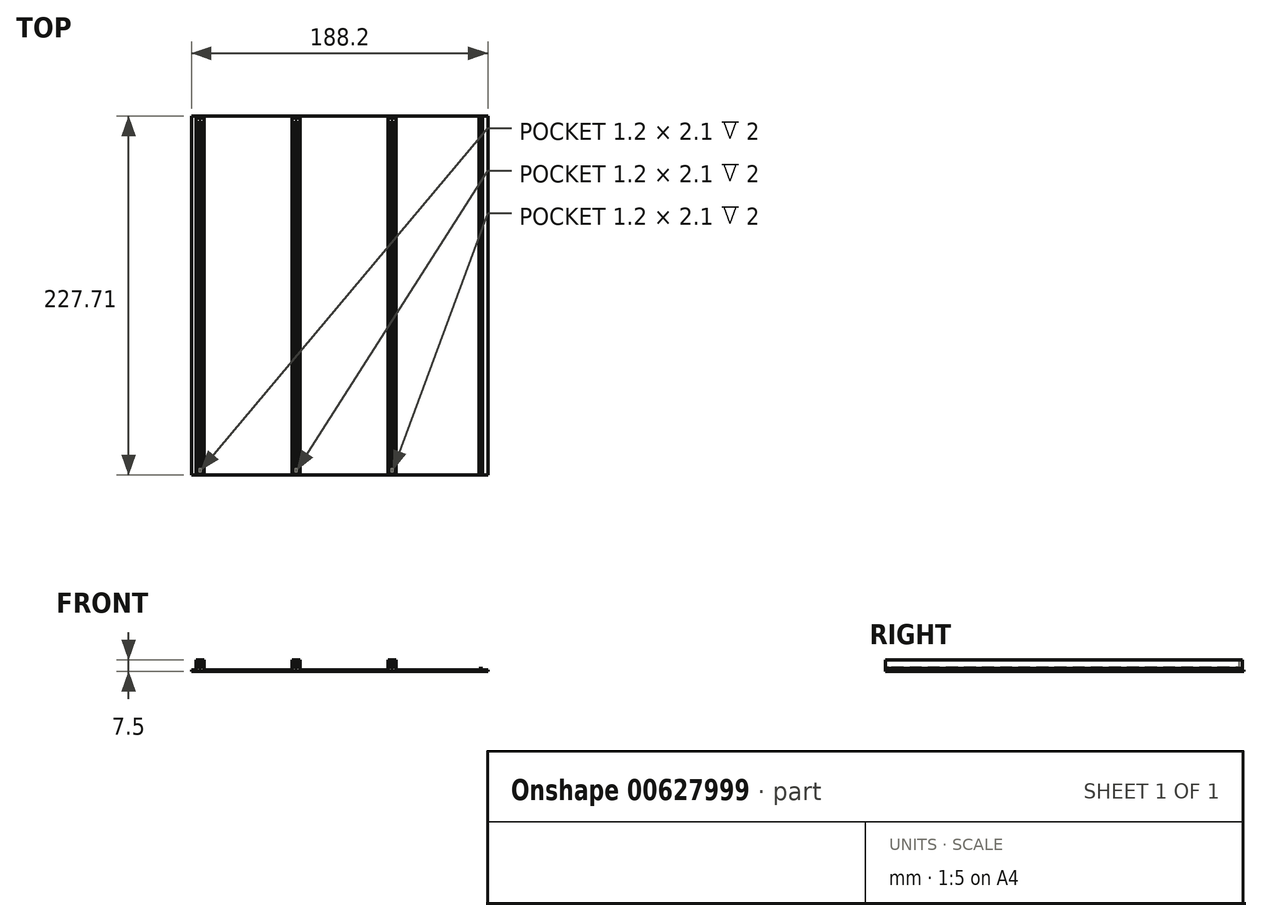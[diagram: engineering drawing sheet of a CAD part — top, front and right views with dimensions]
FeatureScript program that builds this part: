
annotation { "Feature Type Name" : "Feature", "Feature Type Description" : "" }
export const myFeature = defineFeature(function(context is Context, id is Id, definition is map)
    precondition{}
    {
        {
            var Q0;
            Q0=qCreatedBy(makeId("Top.planeOp"),FACE);
            var sketch = newSketch(context, id + "F0", { "sketchPlane" : qUnion([Q0])});
            skLineSegment(sketch, "E0.bottom", {"start": v(0, 0) * mm, "end": v(5.2, 0) * mm});
            skLineSegment(sketch, "E0.top", {"start": v(0, 226.71) * mm, "end": v(5.2, 226.71) * mm});
            skLineSegment(sketch, "E0.left", {"start": v(0, 0) * mm, "end": v(0, 226.71) * mm});
            skLineSegment(sketch, "E0.right", {"start": v(5.2, 0) * mm, "end": v(5.2, 226.71) * mm});
            skLineSegment(sketch, "E1.1.0.0", {"start": v(66.2, 0) * mm, "end": v(66.2, 226.71) * mm});
            skLineSegment(sketch, "E1.1.0.1", {"start": v(61, 0) * mm, "end": v(61, 226.71) * mm});
            skLineSegment(sketch, "E1.1.0.2", {"start": v(61, 226.71) * mm, "end": v(66.2, 226.71) * mm});
            skLineSegment(sketch, "E1.1.0.3", {"start": v(61, 0) * mm, "end": v(66.2, 0) * mm});
            skLineSegment(sketch, "E1.2.0.0", {"start": v(127.2, 0) * mm, "end": v(127.2, 226.71) * mm});
            skLineSegment(sketch, "E1.2.0.1", {"start": v(122, 0) * mm, "end": v(122, 226.71) * mm});
            skLineSegment(sketch, "E1.2.0.2", {"start": v(122, 226.71) * mm, "end": v(127.2, 226.71) * mm});
            skLineSegment(sketch, "E1.2.0.3", {"start": v(122, 0) * mm, "end": v(127.2, 0) * mm});
            skLineSegment(sketch, "E1.direction1", {"start": v(0, 0) * mm, "end": v(61, 0) * mm, "construction": true});
            skSolve(sketch);
        }
        {
            var Q0;
            Q0=makeQuery(id+"F0.imprint","IMPRINT",FACE,{"disambiguationData":[TD([[makeQuery(id+"F0.imprint","IMPRINT",EDGE,{"derivedFrom":sQuery(id+"F0.wireOp",EDGE,"E0.bottom")}),1.0]])]});
            var Q1;
            Q1=makeQuery(id+"F0.imprint","IMPRINT",FACE,{"disambiguationData":[TD([[makeQuery(id+"F0.imprint","IMPRINT",EDGE,{"derivedFrom":sQuery(id+"F0.wireOp",EDGE,"E1.1.0.0")}),1.0]])]});
            var Q2;
            Q2=makeQuery(id+"F0.imprint","IMPRINT",FACE,{"disambiguationData":[TD([[makeQuery(id+"F0.imprint","IMPRINT",EDGE,{"derivedFrom":sQuery(id+"F0.wireOp",EDGE,"E1.2.0.0")}),1.0]])]});
            extrude(context, id + "F1", {"entities" : qUnion([Q0, Q1, Q2]), "depth" : 2 * mm, "offsetDistance" : 25 * mm});
        }
        {
            var Q0;
            Q0=makeQuery(id+"F1.opExtrude","CAP_FACE",FACE,{"disambiguationData":[OSD([sQuery(id+"F0.wireOp",EDGE,"E0.bottom"),sQuery(id+"F0.wireOp",EDGE,"E0.top"),sQuery(id+"F0.wireOp",EDGE,"E0.left"),sQuery(id+"F0.wireOp",EDGE,"E0.right")])],"isStart":false});
            var sketch = newSketch(context, id + "F2", { "sketchPlane" : qUnion([Q0])});
            skLineSegment(sketch, "E2.bottom", {"start": v(0, 0) * mm, "end": v(2, 0) * mm});
            skLineSegment(sketch, "E2.top", {"start": v(0, 226.71) * mm, "end": v(5.2, 226.71) * mm});
            skLineSegment(sketch, "E2.left", {"start": v(0, 0) * mm, "end": v(0, 226.71) * mm});
            skLineSegment(sketch, "E2.right", {"start": v(5.2, 0) * mm, "end": v(5.2, 226.71) * mm});
            skLineSegment(sketch, "E3.top", {"start": v(2, 224.71) * mm, "end": v(3.2, 224.71) * mm});
            skLineSegment(sketch, "E3.left", {"start": v(2, 0) * mm, "end": v(2, 224.71) * mm});
            skLineSegment(sketch, "E3.right", {"start": v(3.2, 0) * mm, "end": v(3.2, 224.71) * mm});
            skLineSegment(sketch, "E4.trimOffspring", {"start": v(3.2, 0) * mm, "end": v(5.2, 0) * mm});
            skLineSegment(sketch, "E5.1.0.0", {"start": v(61, 0) * mm, "end": v(61, 226.71) * mm});
            skLineSegment(sketch, "E5.1.0.1", {"start": v(66.2, 0) * mm, "end": v(66.2, 226.71) * mm});
            skLineSegment(sketch, "E5.1.0.2", {"start": v(63, 0) * mm, "end": v(63, 224.71) * mm});
            skLineSegment(sketch, "E5.1.0.3", {"start": v(64.2, 0) * mm, "end": v(64.2, 224.71) * mm});
            skLineSegment(sketch, "E5.1.0.4", {"start": v(64.2, 0) * mm, "end": v(66.2, 0) * mm});
            skLineSegment(sketch, "E5.1.0.5", {"start": v(61, 226.71) * mm, "end": v(66.2, 226.71) * mm});
            skLineSegment(sketch, "E5.1.0.6", {"start": v(61, 0) * mm, "end": v(63, 0) * mm});
            skLineSegment(sketch, "E5.1.0.7", {"start": v(63, 224.71) * mm, "end": v(64.2, 224.71) * mm});
            skLineSegment(sketch, "E5.2.0.0", {"start": v(122, 0) * mm, "end": v(122, 226.71) * mm});
            skLineSegment(sketch, "E5.2.0.1", {"start": v(127.2, 0) * mm, "end": v(127.2, 226.71) * mm});
            skLineSegment(sketch, "E5.2.0.2", {"start": v(124, 0) * mm, "end": v(124, 224.71) * mm});
            skLineSegment(sketch, "E5.2.0.3", {"start": v(125.2, 0) * mm, "end": v(125.2, 224.71) * mm});
            skLineSegment(sketch, "E5.2.0.4", {"start": v(125.2, 0) * mm, "end": v(127.2, 0) * mm});
            skLineSegment(sketch, "E5.2.0.5", {"start": v(122, 226.71) * mm, "end": v(127.2, 226.71) * mm});
            skLineSegment(sketch, "E5.2.0.6", {"start": v(122, 0) * mm, "end": v(124, 0) * mm});
            skLineSegment(sketch, "E5.2.0.7", {"start": v(124, 224.71) * mm, "end": v(125.2, 224.71) * mm});
            skLineSegment(sketch, "E5.direction1", {"start": v(0, 0) * mm, "end": v(61, 0) * mm, "construction": true});
            skSolve(sketch);
        }
        {
            var Q0;
            Q0=makeQuery(id+"F2.imprint","IMPRINT",FACE,{"disambiguationData":[TD([[makeQuery(id+"F2.imprint","IMPRINT",EDGE,{"derivedFrom":sQuery(id+"F2.wireOp",EDGE,"E2.bottom")}),1.0]])]});
            var Q1;
            Q1=makeQuery(id+"F2.imprint","IMPRINT",FACE,{"disambiguationData":[TD([[makeQuery(id+"F2.imprint","IMPRINT",EDGE,{"derivedFrom":sQuery(id+"F2.wireOp",EDGE,"E5.1.0.0")}),-1.0]])]});
            var Q2;
            Q2=makeQuery(id+"F2.imprint","IMPRINT",FACE,{"disambiguationData":[TD([[makeQuery(id+"F2.imprint","IMPRINT",EDGE,{"derivedFrom":sQuery(id+"F2.wireOp",EDGE,"E5.2.0.0")}),-1.0]])]});
            extrude(context, id + "F3", {"entities" : qUnion([Q0, Q1, Q2]), "operationType" : NewBodyOperationType.ADD, "depth" : 4.5 * mm, "offsetDistance" : 25 * mm});
        }
        {
            var Q0;
            Q0=makeQuery(id+"F1.opExtrude","CAP_FACE",FACE,{"disambiguationData":[OSD([sQuery(id+"F0.wireOp",EDGE,"E0.bottom"),sQuery(id+"F0.wireOp",EDGE,"E0.top"),sQuery(id+"F0.wireOp",EDGE,"E0.left"),sQuery(id+"F0.wireOp",EDGE,"E0.right")])],"isStart":false});
            var sketch = newSketch(context, id + "F4", { "sketchPlane" : qUnion([Q0])});
            skLineSegment(sketch, "E6.bottom", {"start": v(2, 1.9) * mm, "end": v(3.2, 1.9) * mm});
            skLineSegment(sketch, "E6.top", {"start": v(2, 4) * mm, "end": v(3.2, 4) * mm});
            skLineSegment(sketch, "E6.left", {"start": v(2, 1.9) * mm, "end": v(2, 4) * mm});
            skLineSegment(sketch, "E6.right", {"start": v(3.2, 1.9) * mm, "end": v(3.2, 4) * mm});
            skLineSegment(sketch, "E7.1.0.0", {"start": v(63, 1.9) * mm, "end": v(64.2, 1.9) * mm});
            skLineSegment(sketch, "E7.1.0.1", {"start": v(63, 1.9) * mm, "end": v(63, 4) * mm});
            skLineSegment(sketch, "E7.1.0.2", {"start": v(63, 4) * mm, "end": v(64.2, 4) * mm});
            skLineSegment(sketch, "E7.1.0.3", {"start": v(64.2, 1.9) * mm, "end": v(64.2, 4) * mm});
            skLineSegment(sketch, "E7.2.0.0", {"start": v(124, 1.9) * mm, "end": v(125.2, 1.9) * mm});
            skLineSegment(sketch, "E7.2.0.1", {"start": v(124, 1.9) * mm, "end": v(124, 4) * mm});
            skLineSegment(sketch, "E7.2.0.2", {"start": v(124, 4) * mm, "end": v(125.2, 4) * mm});
            skLineSegment(sketch, "E7.2.0.3", {"start": v(125.2, 1.9) * mm, "end": v(125.2, 4) * mm});
            skLineSegment(sketch, "E7.direction1", {"start": v(2, 1.9) * mm, "end": v(63, 1.9) * mm, "construction": true});
            skSolve(sketch);
        }
        {
            var Q0;
            Q0=makeQuery(id+"F4.imprint","IMPRINT",FACE,{"disambiguationData":[TD([[makeQuery(id+"F4.imprint","IMPRINT",EDGE,{"derivedFrom":sQuery(id+"F4.wireOp",EDGE,"E6.bottom")}),1.0]])]});
            var Q1;
            Q1=makeQuery(id+"F4.imprint","IMPRINT",FACE,{"disambiguationData":[TD([[makeQuery(id+"F4.imprint","IMPRINT",EDGE,{"derivedFrom":sQuery(id+"F4.wireOp",EDGE,"E7.1.0.0")}),1.0]])]});
            var Q2;
            Q2=makeQuery(id+"F4.imprint","IMPRINT",FACE,{"disambiguationData":[TD([[makeQuery(id+"F4.imprint","IMPRINT",EDGE,{"derivedFrom":sQuery(id+"F4.wireOp",EDGE,"E7.2.0.0")}),1.0]])]});
            extrude(context, id + "F5", {"entities" : qUnion([Q0, Q1, Q2]), "operationType" : NewBodyOperationType.REMOVE, "oppositeDirection" : true, "depth" : 25 * mm, "offsetDistance" : 25 * mm});
        }
        {
            var Q0;
            Q0=qCreatedBy(makeId("Top.planeOp"),FACE);
            var sketch = newSketch(context, id + "F6", { "sketchPlane" : qUnion([Q0])});
            skLineSegment(sketch, "E8.bottom", {"start": v(0, 0) * mm, "end": v(185.5, 0) * mm});
            skLineSegment(sketch, "E8.top", {"start": v(0, 227.71) * mm, "end": v(185.5, 227.71) * mm});
            skLineSegment(sketch, "E8.left", {"start": v(0, 0) * mm, "end": v(0, 227.71) * mm});
            skLineSegment(sketch, "E8.right", {"start": v(185.5, 0) * mm, "end": v(185.5, 227.71) * mm});
            skLineSegment(sketch, "E9.bottom", {"start": v(0, 0) * mm, "end": v(-2.7, 0) * mm});
            skLineSegment(sketch, "E9.top", {"start": v(0, 227.71) * mm, "end": v(-2.7, 227.71) * mm});
            skLineSegment(sketch, "E9.right", {"start": v(-2.7, 0) * mm, "end": v(-2.7, 227.71) * mm});
            skSolve(sketch);
        }
        {
            var Q0;
            Q0=makeQuery(id+"F6.imprint","IMPRINT",FACE,{"disambiguationData":[TD([[makeQuery(id+"F6.imprint","IMPRINT",EDGE,{"derivedFrom":sQuery(id+"F6.wireOp",EDGE,"E8.bottom")}),1.0]])]});
            var Q1;
            Q1=makeQuery(id+"F6.imprint","IMPRINT",FACE,{"disambiguationData":[TD([[makeQuery(id+"F6.imprint","IMPRINT",EDGE,{"derivedFrom":sQuery(id+"F6.wireOp",EDGE,"E9.bottom")}),-1.0]])]});
            extrude(context, id + "F7", {"entities" : qUnion([Q0, Q1]), "operationType" : NewBodyOperationType.ADD, "oppositeDirection" : true, "depth" : 1 * mm, "offsetDistance" : 25 * mm});
        }
        {
            var Q0;
            {var subQ0=sQuery(id+"F6.wireOp",EDGE,"E8.bottom");var subQ1=sQuery(id+"F6.wireOp",EDGE,"E8.top");var subQ2=sQuery(id+"F6.wireOp",EDGE,"E8.left");var subQ3=sQuery(id+"F6.wireOp",EDGE,"E8.right");Q0=makeQuery(id+"F7.boolean.opBoolean","SPLIT",FACE,{"disambiguationData":[TD([makeQuery(id+"F1.opExtrude","SWEPT_FACE",FACE,{"disambiguationData":[OSD([sQuery(id+"F0.wireOp",EDGE,"E0.bottom")])]})])],"derivedFrom":makeQuery(id+"F7.opExtrude","CAP_FACE",FACE,{"disambiguationData":[OSD([subQ0,subQ1,subQ2,subQ3])],"isStart":true})});}
            var sketch = newSketch(context, id + "F8", { "sketchPlane" : qUnion([Q0])});
            skLineSegment(sketch, "E10.bottom", {"start": v(182, 0) * mm, "end": v(180, 0) * mm});
            skLineSegment(sketch, "E10.top", {"start": v(182, 226.62) * mm, "end": v(180, 226.62) * mm});
            skLineSegment(sketch, "E10.left", {"start": v(182, 0) * mm, "end": v(182, 226.62) * mm});
            skLineSegment(sketch, "E10.right", {"start": v(180, 0) * mm, "end": v(180, 226.62) * mm});
            skSolve(sketch);
        }
        {
            var Q0;
            Q0=makeQuery(id+"F8.imprint","IMPRINT",FACE,{"disambiguationData":[TD([[makeQuery(id+"F8.imprint","IMPRINT",EDGE,{"derivedFrom":sQuery(id+"F8.wireOp",EDGE,"E10.bottom")}),1.0]])]});
            extrude(context, id + "F9", {"entities" : qUnion([Q0]), "operationType" : NewBodyOperationType.ADD, "depth" : 1 * mm, "offsetDistance" : 25 * mm});
        }
        {
            var Q0;
            Q0=makeQuery(id+"F1.opExtrude","CAP_EDGE",EDGE,{"disambiguationData":[OSD([sQuery(id+"F0.wireOp",EDGE,"E0.bottom")])],"isStart":false});
            var Q1;
            Q1=makeQuery(id+"F1.opExtrude","CAP_EDGE",EDGE,{"disambiguationData":[OSD([sQuery(id+"F0.wireOp",EDGE,"E1.1.0.3")])],"isStart":false});
            var Q2;
            Q2=makeQuery(id+"F1.opExtrude","CAP_EDGE",EDGE,{"disambiguationData":[OSD([sQuery(id+"F0.wireOp",EDGE,"E1.2.0.3")])],"isStart":false});
            chamfer(context, id + "F10", {"entities" : qUnion([Q0, Q1, Q2]), "width" : 1 * mm, "tangentPropagation" : true});
        }
    });
